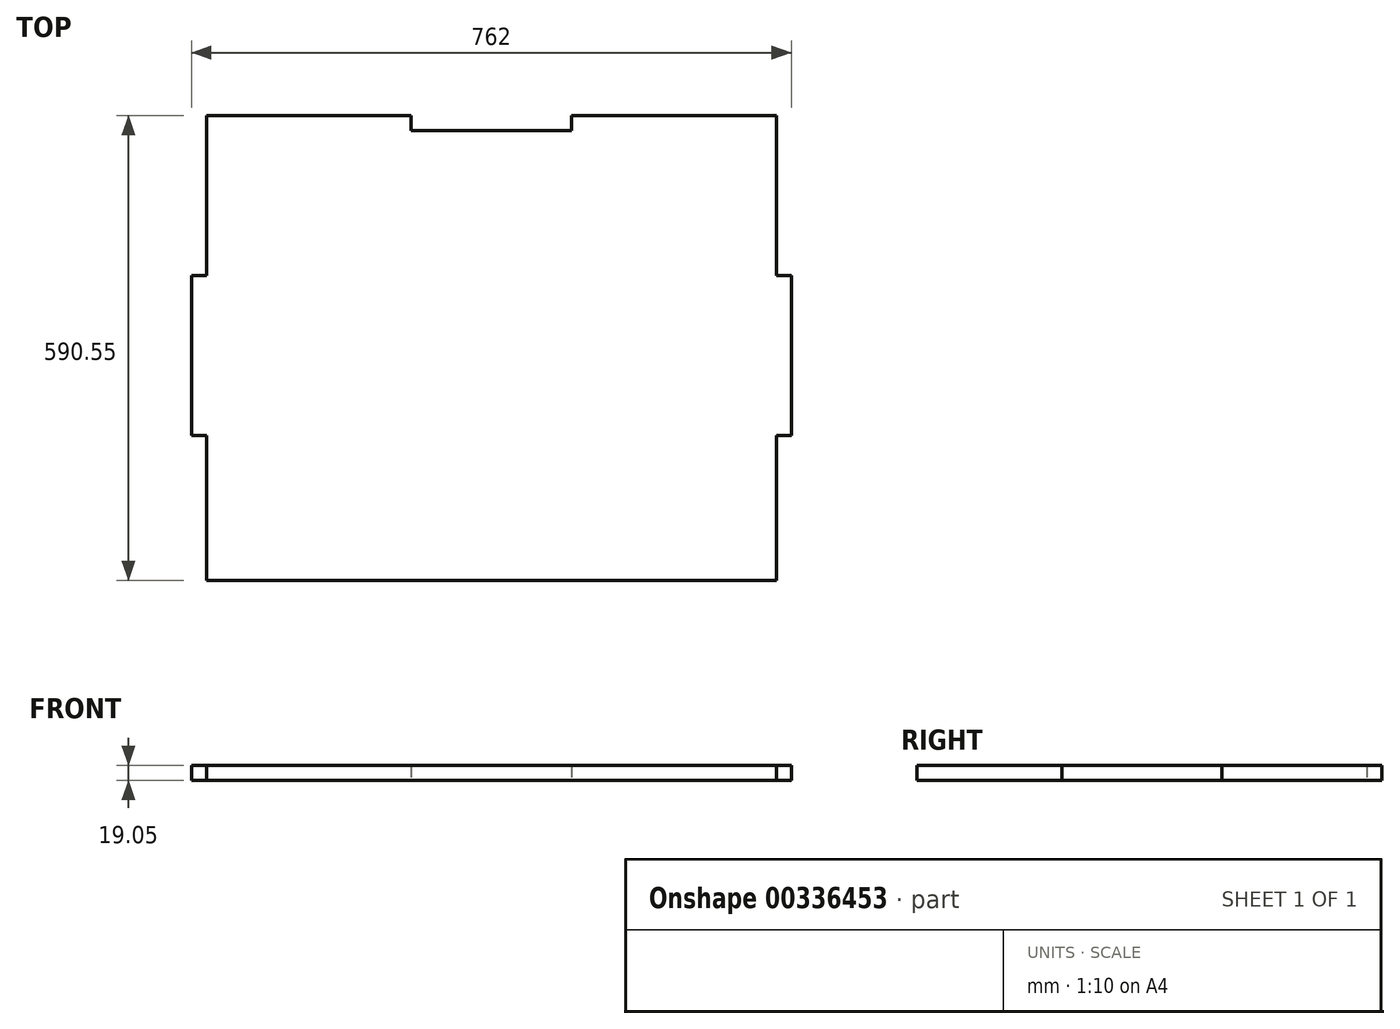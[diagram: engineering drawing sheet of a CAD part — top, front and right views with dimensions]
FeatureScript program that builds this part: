
annotation { "Feature Type Name" : "Feature", "Feature Type Description" : "" }
export const myFeature = defineFeature(function(context is Context, id is Id, definition is map)
    precondition{}
    {
        {
            var Q0;
            Q0=qCreatedBy(makeId("Top.planeOp"),FACE);
            var sketch = newSketch(context, id + "F0", { "sketchPlane" : qUnion([Q0])});
            skLineSegment(sketch, "E0.bottom", {"start": v(-383.6, 404.46) * mm, "end": v(378.4, 404.46) * mm});
            skLineSegment(sketch, "E0.top", {"start": v(-383.6, -205.14) * mm, "end": v(378.4, -205.14) * mm});
            skLineSegment(sketch, "E0.left", {"start": v(-383.6, 404.46) * mm, "end": v(-383.6, -205.14) * mm});
            skLineSegment(sketch, "E0.right", {"start": v(378.4, 404.46) * mm, "end": v(378.4, -205.14) * mm});
            skLineSegment(sketch, "E1.bottom", {"start": v(-364.54, -1.94) * mm, "end": v(-383.6, -1.94) * mm});
            skLineSegment(sketch, "E1.top", {"start": v(-364.54, 201.26) * mm, "end": v(-383.6, 201.26) * mm});
            skLineSegment(sketch, "E1.left", {"start": v(-364.54, -1.94) * mm, "end": v(-364.54, 201.26) * mm});
            skLineSegment(sketch, "E1.right", {"start": v(-383.6, -1.94) * mm, "end": v(-383.6, 201.26) * mm});
            skPoint(sketch, "E1.middle", {"position": v(-374.07, 99.66) * mm});
            skLineSegment(sketch, "E2", {"start": v(-364.54, 201.26) * mm, "end": v(-364.54, 404.46) * mm});
            skLineSegment(sketch, "E3", {"start": v(-364.54, -1.94) * mm, "end": v(-364.54, -205.14) * mm});
            skLineSegment(sketch, "E4.bottom", {"start": v(378.4, -1.94) * mm, "end": v(359.36, -1.94) * mm});
            skLineSegment(sketch, "E4.top", {"start": v(378.4, 201.26) * mm, "end": v(359.36, 201.26) * mm});
            skLineSegment(sketch, "E4.left", {"start": v(378.4, -1.94) * mm, "end": v(378.4, 201.26) * mm});
            skLineSegment(sketch, "E4.right", {"start": v(359.36, -1.94) * mm, "end": v(359.36, 201.26) * mm});
            skPoint(sketch, "E4.middle", {"position": v(368.88, 99.66) * mm});
            skLineSegment(sketch, "E5", {"start": v(359.36, 201.26) * mm, "end": v(359.36, 404.46) * mm});
            skLineSegment(sketch, "E6", {"start": v(359.36, -1.94) * mm, "end": v(359.36, -205.14) * mm});
            skLineSegment(sketch, "E7.bottom", {"start": v(99, 385.4) * mm, "end": v(-104.2, 385.4) * mm});
            skLineSegment(sketch, "E7.top", {"start": v(99, 404.46) * mm, "end": v(-104.2, 404.46) * mm});
            skLineSegment(sketch, "E7.left", {"start": v(99, 385.4) * mm, "end": v(99, 404.46) * mm});
            skLineSegment(sketch, "E7.right", {"start": v(-104.2, 385.4) * mm, "end": v(-104.2, 404.46) * mm});
            skPoint(sketch, "E7.middle", {"position": v(-2.6, 394.93) * mm});
            skLineSegment(sketch, "E8.bottom", {"start": v(99, -205.14) * mm, "end": v(-104.2, -205.14) * mm});
            skLineSegment(sketch, "E8.top", {"start": v(99, -186.1) * mm, "end": v(-104.2, -186.1) * mm});
            skLineSegment(sketch, "E8.left", {"start": v(99, -205.14) * mm, "end": v(99, -186.1) * mm});
            skLineSegment(sketch, "E8.right", {"start": v(-104.2, -205.14) * mm, "end": v(-104.2, -186.1) * mm});
            skPoint(sketch, "E8.middle", {"position": v(-2.6, -195.62) * mm});
            skLineSegment(sketch, "E9", {"start": v(-104.2, -186.1) * mm, "end": v(-383.6, -186.1) * mm});
            skLineSegment(sketch, "E10", {"start": v(99, -186.1) * mm, "end": v(378.4, -186.1) * mm});
            skSolve(sketch);
        }
        {
            var Q0;
            Q0=makeQuery(id+"F0.imprint","IMPRINT",FACE,{"disambiguationData":[TD([[makeQuery(id+"F0.imprint","IMPRINT",EDGE,{"derivedFrom":sQuery(id+"F0.wireOp",EDGE,"E1.bottom")}),-1.0]])]});
            var Q1;
            Q1=makeQuery(id+"F0.imprint","IMPRINT",FACE,{"disambiguationData":[TD([[makeQuery(id+"F0.imprint","IMPRINT",EDGE,{"derivedFrom":sQuery(id+"F0.wireOp",EDGE,"E1.left")}),-1.0]])]});
            var Q2;
            Q2=makeQuery(id+"F0.imprint","IMPRINT",FACE,{"disambiguationData":[TD([[makeQuery(id+"F0.imprint","IMPRINT",EDGE,{"derivedFrom":sQuery(id+"F0.wireOp",EDGE,"E4.bottom")}),-1.0]])]});
            var Q3;
            Q3=makeQuery(id+"F0.imprint","IMPRINT",FACE,{"disambiguationData":[TD([[makeQuery(id+"F0.imprint","IMPRINT",EDGE,{"derivedFrom":sQuery(id+"F0.wireOp",EDGE,"E8.bottom")}),-1.0]])]});
            extrude(context, id + "F1", {"entities" : qUnion([Q0, Q1, Q2, Q3]), "depth" : 19.05 * mm});
        }
    });
